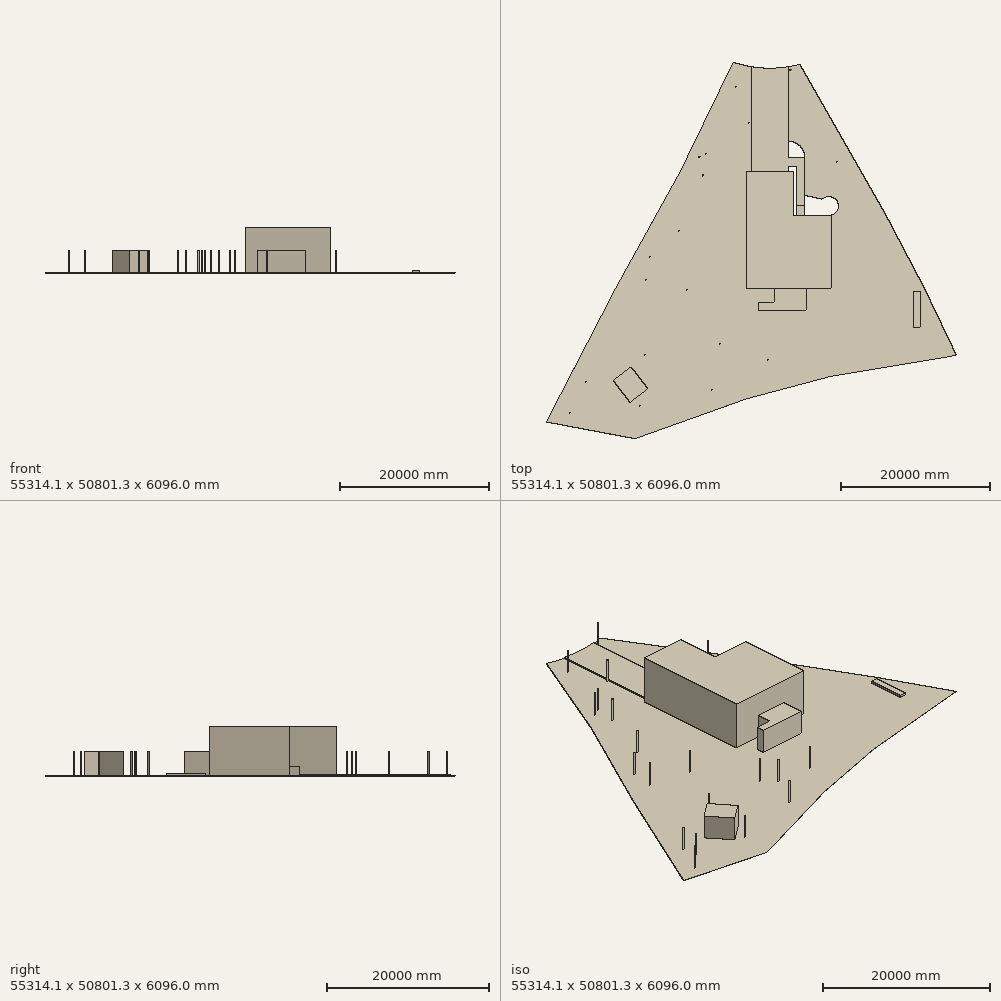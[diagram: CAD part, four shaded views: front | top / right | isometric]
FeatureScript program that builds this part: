
annotation { "Feature Type Name" : "Feature", "Feature Type Description" : "" }
export const myFeature = defineFeature(function(context is Context, id is Id, definition is map)
    precondition{}
    {
        {
            var Q0;
            Q0=qCreatedBy(makeId("Top.planeOp"),FACE);
            var sketch = newSketch(context, id + "F0", { "sketchPlane" : qUnion([Q0])});
            skLineSegment(sketch, "E0.top", {"start": v(-3124.2, -13967.14) * mm, "end": v(3124.2, -13967.14) * mm});
            skLineSegment(sketch, "E0.left", {"start": v(-2514.6, 206.06) * mm, "end": v(-2514.6, -13967.14) * mm});
            skLineSegment(sketch, "E0.right", {"start": v(2514.6, 206.06) * mm, "end": v(2514.6, -13967.14) * mm});
            skLineSegment(sketch, "E1", {"start": v(2514.6, -13205.14) * mm, "end": v(3581.4, -13205.14) * mm});
            skLineSegment(sketch, "E2", {"start": v(3581.4, -13205.14) * mm, "end": v(3581.4, -18539.14) * mm});
            skLineSegment(sketch, "E3", {"start": v(3124.2, -13967.14) * mm, "end": v(3124.2, -19809.14) * mm});
            skLineSegment(sketch, "E4", {"start": v(2514.6, -11985.94) * mm, "end": v(4648.2, -11985.94) * mm});
            skLineSegment(sketch, "E5", {"start": v(4648.2, -11985.94) * mm, "end": v(4648.2, -18539.14) * mm});
            skArc(sketch, "E6", {"start": v(4648.2, -11985.94) * mm, "mid": v(4023.28, -10477.26) * mm, "end": v(2514.6, -9852.34) * mm});
            skLineSegment(sketch, "E7", {"start": v(3581.4, -18539.14) * mm, "end": v(4648.2, -18539.14) * mm});
            skLineSegment(sketch, "E8", {"start": v(4648.2, -17142.14) * mm, "end": v(7068.85, -17675.54) * mm});
            skLineSegment(sketch, "E9", {"start": v(3581.4, -18539.14) * mm, "end": v(3581.4, -19809.14) * mm});
            skLineSegment(sketch, "E10", {"start": v(3124.2, -19809.14) * mm, "end": v(8305.8, -19809.14) * mm});
            skLineSegment(sketch, "E11", {"start": v(4648.2, -19809.14) * mm, "end": v(4648.2, -18539.14) * mm});
            skArc(sketch, "E12", {"start": v(8305.8, -19809.14) * mm, "mid": v(9048.91, -17952.97) * mm, "end": v(7068.85, -17675.54) * mm});
            skLineSegment(sketch, "E13", {"start": v(8305.8, -19809.14) * mm, "end": v(8305.8, -17370.74) * mm, "construction": true});
            skLineSegment(sketch, "E14", {"start": v(8305.8, -18589.94) * mm, "end": v(9220.2, -18589.94) * mm, "construction": true});
            skLineSegment(sketch, "E15", {"start": v(8305.8, -19809.14) * mm, "end": v(15621, -19809.14) * mm, "construction": true});
            skLineSegment(sketch, "E16", {"start": v(-2514.6, 206.06) * mm, "end": v(2514.6, 206.06) * mm, "construction": true});
            skPoint(sketch, "E17", {"position": v(9020.95, -12627.77) * mm});
            skLineSegment(sketch, "E18", {"start": v(8305.8, -19809.14) * mm, "end": v(8305.8, -29664.34) * mm});
            skLineSegment(sketch, "E19", {"start": v(8305.8, -29664.34) * mm, "end": v(20802.6, -29664.34) * mm, "construction": true});
            skLineSegment(sketch, "E20", {"start": v(20802.6, -29664.34) * mm, "end": v(15621, -19809.14) * mm});
            skLineSegment(sketch, "E21", {"start": v(8305.8, -29664.34) * mm, "end": v(8305.8, -41551.54) * mm, "construction": true});
            skLineSegment(sketch, "E22", {"start": v(8305.8, -41551.54) * mm, "end": v(25141.27, -38738.88) * mm});
            skLineSegment(sketch, "E23", {"start": v(25141.27, -38738.88) * mm, "end": v(20802.6, -29664.34) * mm});
            skLineSegment(sketch, "E24.bottom", {"start": v(20225.87, -30162.36) * mm, "end": v(19362.27, -30162.36) * mm});
            skLineSegment(sketch, "E24.top", {"start": v(20225.87, -35039.16) * mm, "end": v(19362.27, -35039.16) * mm});
            skLineSegment(sketch, "E24.left", {"start": v(20225.87, -30162.36) * mm, "end": v(20225.87, -35039.16) * mm});
            skLineSegment(sketch, "E24.right", {"start": v(19362.27, -30162.36) * mm, "end": v(19362.27, -35039.16) * mm});
            skArc(sketch, "E25", {"start": v(-4953, 815.66) * mm, "mid": v(-495.72, 7.96) * mm, "end": v(4004.2, 528.05) * mm});
            skLineSegment(sketch, "E26", {"start": v(0, 206.06) * mm, "end": v(0, 0) * mm, "construction": true});
            skLineSegment(sketch, "E27", {"start": v(-4953, 815.66) * mm, "end": v(-12115.8, -13967.14) * mm});
            skLineSegment(sketch, "E28", {"start": v(-4953, 815.66) * mm, "end": v(-4953, 206.06) * mm, "construction": true});
            skLineSegment(sketch, "E29", {"start": v(-4953, 206.06) * mm, "end": v(-2514.6, 206.06) * mm, "construction": true});
            skLineSegment(sketch, "E30", {"start": v(4004.2, 528.05) * mm, "end": v(15621, -19809.14) * mm});
            skPoint(sketch, "E31", {"position": v(2743.2, -251.14) * mm});
            skPoint(sketch, "E32", {"position": v(-9525, -11985.94) * mm});
            skPoint(sketch, "E33", {"position": v(-8610.6, -11528.74) * mm});
            skPoint(sketch, "E34", {"position": v(-2819.4, -7413.94) * mm});
            skPoint(sketch, "E35", {"position": v(-4648.2, -2537.14) * mm});
            skLineSegment(sketch, "E36", {"start": v(-12115.8, -13967.14) * mm, "end": v(-3124.2, -13967.14) * mm, "construction": true});
            skLineSegment(sketch, "E37", {"start": v(-3124.2, -13967.14) * mm, "end": v(-3124.2, -29664.34) * mm});
            skLineSegment(sketch, "E38", {"start": v(-3124.2, -29664.34) * mm, "end": v(8305.8, -29664.34) * mm});
            skLineSegment(sketch, "E39", {"start": v(-12115.8, -13967.14) * mm, "end": v(-20802.6, -29664.34) * mm});
            skLineSegment(sketch, "E40", {"start": v(-20802.6, -29664.34) * mm, "end": v(-3124.2, -29664.34) * mm, "construction": true});
            skPoint(sketch, "E41", {"position": v(-9046.4, -14470.95) * mm});
            skPoint(sketch, "E42", {"position": v(-12253.47, -21932.63) * mm});
            skPoint(sketch, "E43", {"position": v(-16258.55, -25455.58) * mm});
            skPoint(sketch, "E44", {"position": v(-16721.27, -28585.52) * mm});
            skPoint(sketch, "E45", {"position": v(-11198.91, -29864.83) * mm});
            skLineSegment(sketch, "E46", {"start": v(-3124.2, -29664.34) * mm, "end": v(-3124.2, -44599.54) * mm, "construction": true});
            skLineSegment(sketch, "E47", {"start": v(-3124.2, -44599.54) * mm, "end": v(8305.8, -41551.54) * mm});
            skLineSegment(sketch, "E48", {"start": v(533.4, -29664.34) * mm, "end": v(533.4, -31645.54) * mm});
            skLineSegment(sketch, "E49", {"start": v(533.4, -31645.54) * mm, "end": v(-1600.2, -31645.54) * mm});
            skLineSegment(sketch, "E50", {"start": v(-1600.2, -31645.54) * mm, "end": v(-1600.2, -32712.34) * mm});
            skLineSegment(sketch, "E51", {"start": v(-1600.2, -32712.34) * mm, "end": v(4876.8, -32712.34) * mm});
            skLineSegment(sketch, "E52", {"start": v(4876.8, -32712.34) * mm, "end": v(4876.8, -29664.34) * mm});
            skPoint(sketch, "E53", {"position": v(-324.1, -39325.13) * mm});
            skLineSegment(sketch, "E54", {"start": v(-20802.6, -29664.34) * mm, "end": v(-30172.82, -47723.53) * mm});
            skLineSegment(sketch, "E55", {"start": v(-30172.82, -47723.53) * mm, "end": v(-18192.51, -49985.63) * mm});
            skLineSegment(sketch, "E56", {"start": v(-18192.51, -49985.63) * mm, "end": v(-3124.2, -44599.54) * mm});
            skLineSegment(sketch, "E57.bottom", {"start": v(-18746, -40298.2) * mm, "end": v(-16470.03, -43258.14) * mm});
            skLineSegment(sketch, "E57.top", {"start": v(-21162.27, -42156.12) * mm, "end": v(-18886.3, -45116.06) * mm});
            skLineSegment(sketch, "E57.left", {"start": v(-18746, -40298.2) * mm, "end": v(-21162.27, -42156.12) * mm});
            skLineSegment(sketch, "E57.right", {"start": v(-16470.03, -43258.14) * mm, "end": v(-18886.3, -45116.06) * mm});
            skPoint(sketch, "E58", {"position": v(-24816.9, -42303.32) * mm});
            skPoint(sketch, "E59", {"position": v(-24787.94, -44406.35) * mm});
            skPoint(sketch, "E60", {"position": v(-27054.85, -46490.83) * mm});
            skPoint(sketch, "E61", {"position": v(-17599.17, -45589.94) * mm});
            skPoint(sketch, "E62", {"position": v(-16859.27, -38733.7) * mm});
            skPoint(sketch, "E63", {"position": v(-7839.03, -43353.12) * mm});
            skPoint(sketch, "E64", {"position": v(-6760.12, -37216.7) * mm});
            skPoint(sketch, "E65", {"position": v(-5224.45, -38876.76) * mm});
            skCircle(sketch, "E66", {"center": v(-2819.4, -7413.94) * mm, "radius": 76.2 * mm});
            skCircle(sketch, "E67", {"center": v(-4648.2, -2537.14) * mm, "radius": 76.2 * mm});
            skCircle(sketch, "E68", {"center": v(-8610.6, -11528.74) * mm, "radius": 76.2 * mm});
            skCircle(sketch, "E69", {"center": v(-9525, -11985.94) * mm, "radius": 76.2 * mm});
            skCircle(sketch, "E70", {"center": v(-9046.4, -14470.95) * mm, "radius": 76.2 * mm});
            skCircle(sketch, "E71", {"center": v(-12253.47, -21932.63) * mm, "radius": 76.2 * mm});
            skCircle(sketch, "E72", {"center": v(-16258.55, -25455.58) * mm, "radius": 76.2 * mm});
            skCircle(sketch, "E73", {"center": v(-16721.27, -28585.52) * mm, "radius": 76.2 * mm});
            skCircle(sketch, "E74", {"center": v(-11198.91, -29864.83) * mm, "radius": 76.2 * mm});
            skCircle(sketch, "E75", {"center": v(-16859.27, -38733.7) * mm, "radius": 76.2 * mm});
            skCircle(sketch, "E76", {"center": v(-24816.9, -42303.32) * mm, "radius": 76.2 * mm});
            skCircle(sketch, "E77", {"center": v(-24787.94, -44406.35) * mm, "radius": 76.2 * mm});
            skCircle(sketch, "E78", {"center": v(-27054.85, -46490.83) * mm, "radius": 76.2 * mm});
            skCircle(sketch, "E79", {"center": v(-17599.17, -45589.94) * mm, "radius": 76.2 * mm});
            skCircle(sketch, "E80", {"center": v(-7839.03, -43353.12) * mm, "radius": 76.2 * mm});
            skCircle(sketch, "E81", {"center": v(-6760.12, -37216.7) * mm, "radius": 76.2 * mm});
            skCircle(sketch, "E82", {"center": v(-5224.45, -38876.76) * mm, "radius": 76.2 * mm});
            skCircle(sketch, "E83", {"center": v(-324.1, -39325.13) * mm, "radius": 76.2 * mm});
            skCircle(sketch, "E84", {"center": v(9020.95, -12627.77) * mm, "radius": 76.2 * mm});
            skCircle(sketch, "E85", {"center": v(2743.2, -251.14) * mm, "radius": 76.2 * mm});
            skSolve(sketch);
        }
        {
            var Q0;
            {var subQ7=sQuery(id+"F0.wireOp",EDGE,"E3");Q0=makeQuery(id+"F0.imprint","IMPRINT",FACE,{"disambiguationData":[TD([[makeQuery(id+"F0.imprint","IMPRINT",EDGE,{"derivedFrom":subQ7}),-1.0]])]});}
            extrude(context, id + "F1", {"entities" : qUnion([Q0]), "depth" : 6096 * mm, "offsetDistance" : 30.48 * mm});
        }
        {
            var Q0;
            {var subQ5=sQuery(id+"F0.wireOp",EDGE,"E0.left");Q0=makeQuery(id+"F0.imprint","IMPRINT",FACE,{"disambiguationData":[TD([[makeQuery(id+"F0.imprint","IMPRINT",EDGE,{"derivedFrom":subQ5}),1.0]])]});}
            var Q1;
            {var subQ0=sQuery(id+"F0.wireOp",EDGE,"E1");Q1=makeQuery(id+"F0.imprint","IMPRINT",FACE,{"disambiguationData":[TD([[makeQuery(id+"F0.imprint","IMPRINT",EDGE,{"derivedFrom":subQ0}),1.0]])]});}
            extrude(context, id + "F2", {"entities" : qUnion([Q0, Q1]), "operationType" : NewBodyOperationType.ADD, "depth" : 152.4 * mm, "offsetDistance" : 30.48 * mm});
        }
        {
            var Q0;
            Q0=makeQuery(id+"F0.imprint","IMPRINT",FACE,{"disambiguationData":[TD([[makeQuery(id+"F0.imprint","IMPRINT",EDGE,{"derivedFrom":sQuery(id+"F0.wireOp",EDGE,"E7")}),-1.0]])]});
            extrude(context, id + "F3", {"entities" : qUnion([Q0]), "operationType" : NewBodyOperationType.ADD, "depth" : 1219.2 * mm, "offsetDistance" : 30.48 * mm});
        }
        {
            var Q0;
            {var subQ0=sQuery(id+"F0.wireOp",EDGE,"E48");Q0=makeQuery(id+"F0.imprint","IMPRINT",FACE,{"disambiguationData":[TD([[makeQuery(id+"F0.imprint","IMPRINT",EDGE,{"derivedFrom":subQ0}),1.0]])]});}
            extrude(context, id + "F4", {"entities" : qUnion([Q0]), "operationType" : NewBodyOperationType.ADD, "depth" : 3048 * mm, "offsetDistance" : 30.48 * mm});
        }
        {
            var Q0;
            Q0=makeQuery(id+"F0.imprint","IMPRINT",FACE,{"disambiguationData":[TD([[makeQuery(id+"F0.imprint","IMPRINT",EDGE,{"derivedFrom":sQuery(id+"F0.wireOp",EDGE,"E57.bottom")}),-1.0]])]});
            extrude(context, id + "F5", {"entities" : qUnion([Q0]), "depth" : 3048 * mm, "offsetDistance" : 30.48 * mm});
        }
        {
            var Q0;
            Q0=makeQuery(id+"F0.imprint","IMPRINT",FACE,{"disambiguationData":[TD([[makeQuery(id+"F0.imprint","IMPRINT",EDGE,{"derivedFrom":sQuery(id+"F0.wireOp",EDGE,"E24.bottom")}),1.0]])]});
            extrude(context, id + "F6", {"entities" : qUnion([Q0]), "depth" : 304.8 * mm, "offsetDistance" : 30.48 * mm});
        }
        {
            var Q0;
            {var subQ6=sQuery(id+"F0.wireOp",EDGE,"E0.left");Q0=makeQuery(id+"F0.imprint","IMPRINT",FACE,{"disambiguationData":[TD([[makeQuery(id+"F0.imprint","IMPRINT",EDGE,{"derivedFrom":subQ6}),-1.0]])]});}
            extrude(context, id + "F7", {"entities" : qUnion([Q0]), "depth" : 30.48 * mm, "offsetDistance" : 30.48 * mm});
        }
        {
            var Q0;
            Q0=makeQuery(id+"F0.imprint","IMPRINT",FACE,{"disambiguationData":[TD([[makeQuery(id+"F0.imprint","IMPRINT",EDGE,{"derivedFrom":sQuery(id+"F0.wireOp",EDGE,"E85")}),1.0]])]});
            var Q1;
            Q1=makeQuery(id+"F0.imprint","IMPRINT",FACE,{"disambiguationData":[TD([[makeQuery(id+"F0.imprint","IMPRINT",EDGE,{"derivedFrom":sQuery(id+"F0.wireOp",EDGE,"E84")}),1.0]])]});
            var Q2;
            Q2=makeQuery(id+"F0.imprint","IMPRINT",FACE,{"disambiguationData":[TD([[makeQuery(id+"F0.imprint","IMPRINT",EDGE,{"derivedFrom":sQuery(id+"F0.wireOp",EDGE,"E67")}),1.0]])]});
            var Q3;
            Q3=makeQuery(id+"F0.imprint","IMPRINT",FACE,{"disambiguationData":[TD([[makeQuery(id+"F0.imprint","IMPRINT",EDGE,{"derivedFrom":sQuery(id+"F0.wireOp",EDGE,"E66")}),1.0]])]});
            var Q4;
            Q4=makeQuery(id+"F0.imprint","IMPRINT",FACE,{"disambiguationData":[TD([[makeQuery(id+"F0.imprint","IMPRINT",EDGE,{"derivedFrom":sQuery(id+"F0.wireOp",EDGE,"E68")}),1.0]])]});
            var Q5;
            Q5=makeQuery(id+"F0.imprint","IMPRINT",FACE,{"disambiguationData":[TD([[makeQuery(id+"F0.imprint","IMPRINT",EDGE,{"derivedFrom":sQuery(id+"F0.wireOp",EDGE,"E69")}),1.0]])]});
            var Q6;
            Q6=makeQuery(id+"F0.imprint","IMPRINT",FACE,{"disambiguationData":[TD([[makeQuery(id+"F0.imprint","IMPRINT",EDGE,{"derivedFrom":sQuery(id+"F0.wireOp",EDGE,"E70")}),1.0]])]});
            var Q7;
            Q7=makeQuery(id+"F0.imprint","IMPRINT",FACE,{"disambiguationData":[TD([[makeQuery(id+"F0.imprint","IMPRINT",EDGE,{"derivedFrom":sQuery(id+"F0.wireOp",EDGE,"E71")}),1.0]])]});
            var Q8;
            Q8=makeQuery(id+"F0.imprint","IMPRINT",FACE,{"disambiguationData":[TD([[makeQuery(id+"F0.imprint","IMPRINT",EDGE,{"derivedFrom":sQuery(id+"F0.wireOp",EDGE,"E72")}),1.0]])]});
            var Q9;
            Q9=makeQuery(id+"F0.imprint","IMPRINT",FACE,{"disambiguationData":[TD([[makeQuery(id+"F0.imprint","IMPRINT",EDGE,{"derivedFrom":sQuery(id+"F0.wireOp",EDGE,"E73")}),1.0]])]});
            var Q10;
            Q10=makeQuery(id+"F0.imprint","IMPRINT",FACE,{"disambiguationData":[TD([[makeQuery(id+"F0.imprint","IMPRINT",EDGE,{"derivedFrom":sQuery(id+"F0.wireOp",EDGE,"E74")}),1.0]])]});
            var Q11;
            Q11=makeQuery(id+"F0.imprint","IMPRINT",FACE,{"disambiguationData":[TD([[makeQuery(id+"F0.imprint","IMPRINT",EDGE,{"derivedFrom":sQuery(id+"F0.wireOp",EDGE,"E78")}),1.0]])]});
            var Q12;
            Q12=makeQuery(id+"F0.imprint","IMPRINT",FACE,{"disambiguationData":[TD([[makeQuery(id+"F0.imprint","IMPRINT",EDGE,{"derivedFrom":sQuery(id+"F0.wireOp",EDGE,"E77")}),1.0]])]});
            var Q13;
            Q13=makeQuery(id+"F0.imprint","IMPRINT",FACE,{"disambiguationData":[TD([[makeQuery(id+"F0.imprint","IMPRINT",EDGE,{"derivedFrom":sQuery(id+"F0.wireOp",EDGE,"E76")}),1.0]])]});
            var Q14;
            Q14=makeQuery(id+"F0.imprint","IMPRINT",FACE,{"disambiguationData":[TD([[makeQuery(id+"F0.imprint","IMPRINT",EDGE,{"derivedFrom":sQuery(id+"F0.wireOp",EDGE,"E79")}),1.0]])]});
            var Q15;
            Q15=makeQuery(id+"F0.imprint","IMPRINT",FACE,{"disambiguationData":[TD([[makeQuery(id+"F0.imprint","IMPRINT",EDGE,{"derivedFrom":sQuery(id+"F0.wireOp",EDGE,"E75")}),1.0]])]});
            var Q16;
            Q16=makeQuery(id+"F0.imprint","IMPRINT",FACE,{"disambiguationData":[TD([[makeQuery(id+"F0.imprint","IMPRINT",EDGE,{"derivedFrom":sQuery(id+"F0.wireOp",EDGE,"E80")}),1.0]])]});
            var Q17;
            Q17=makeQuery(id+"F0.imprint","IMPRINT",FACE,{"disambiguationData":[TD([[makeQuery(id+"F0.imprint","IMPRINT",EDGE,{"derivedFrom":sQuery(id+"F0.wireOp",EDGE,"E81")}),1.0]])]});
            var Q18;
            Q18=makeQuery(id+"F0.imprint","IMPRINT",FACE,{"disambiguationData":[TD([[makeQuery(id+"F0.imprint","IMPRINT",EDGE,{"derivedFrom":sQuery(id+"F0.wireOp",EDGE,"E82")}),1.0]])]});
            var Q19;
            Q19=makeQuery(id+"F0.imprint","IMPRINT",FACE,{"disambiguationData":[TD([[makeQuery(id+"F0.imprint","IMPRINT",EDGE,{"derivedFrom":sQuery(id+"F0.wireOp",EDGE,"E83")}),1.0]])]});
            extrude(context, id + "F8", {"entities" : qUnion([Q0, Q1, Q2, Q3, Q4, Q5, Q6, Q7, Q8, Q9, Q10, Q11, Q12, Q13, Q14, Q15, Q16, Q17, Q18, Q19]), "operationType" : NewBodyOperationType.ADD, "depth" : 3048 * mm, "offsetDistance" : 30.48 * mm});
        }
    });
